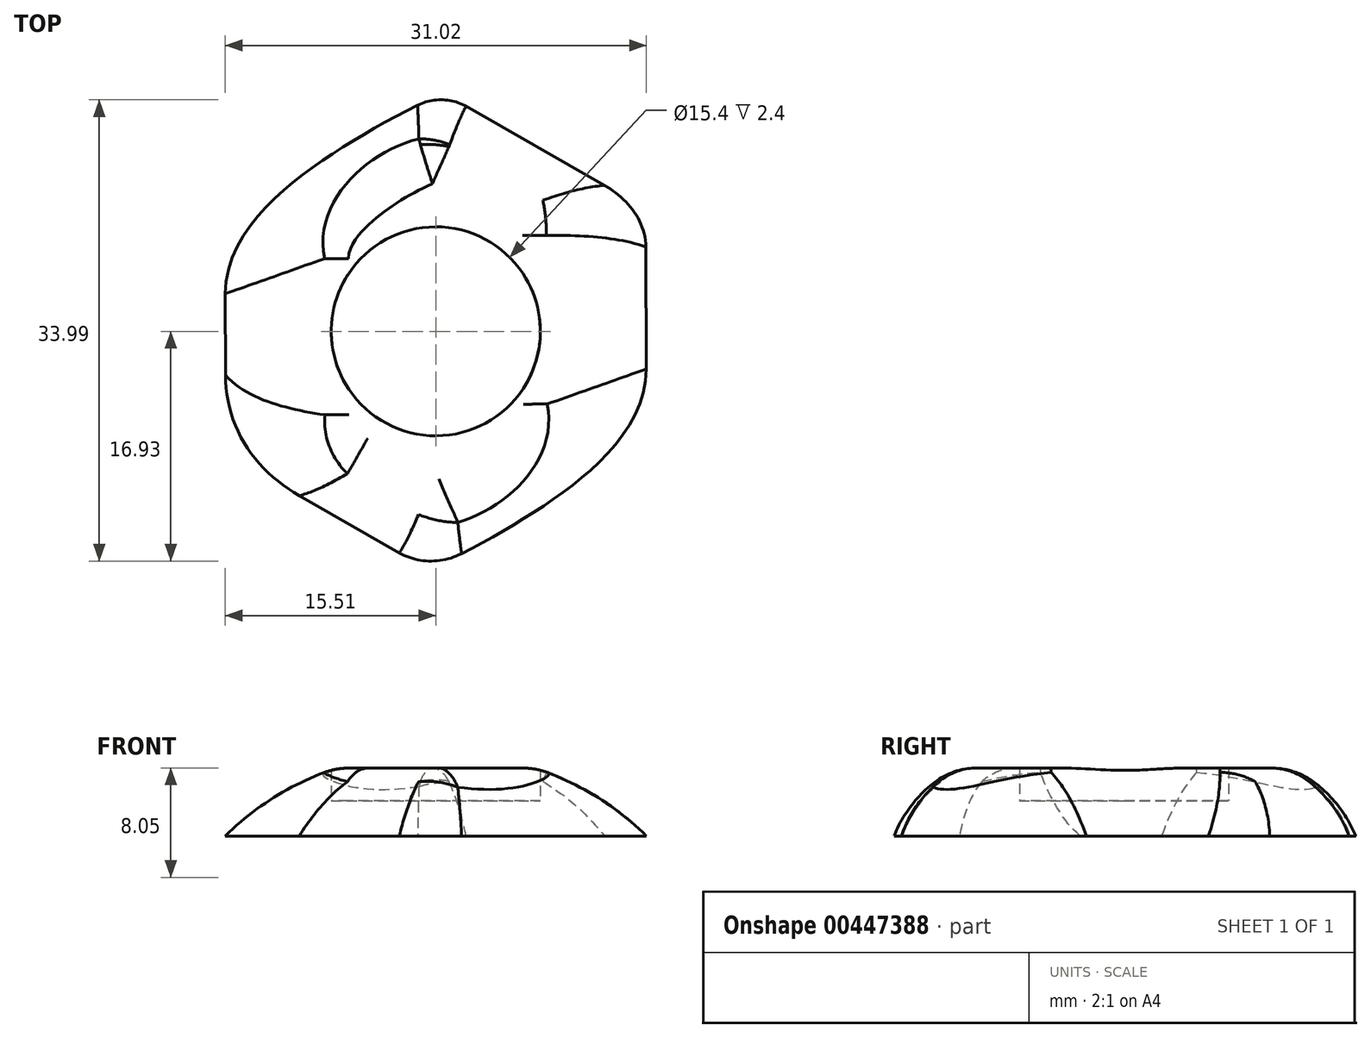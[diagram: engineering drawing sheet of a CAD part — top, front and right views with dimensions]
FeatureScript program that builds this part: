
annotation { "Feature Type Name" : "Feature", "Feature Type Description" : "" }
export const myFeature = defineFeature(function(context is Context, id is Id, definition is map)
    precondition{}
    {
        {
            var Q0;
            Q0=qCreatedBy(makeId("Top.planeOp"),FACE);
            var sketch = newSketch(context, id + "F0", { "sketchPlane" : qUnion([Q0])});
            skCircle(sketch, "E0.cCircle", {"center": v(0, 0) * mm, "radius": 17.9 * mm, "construction": true});
            skLineSegment(sketch, "E0.0", {"start": v(-15.53, 8.9) * mm, "end": v(-0.06, 17.9) * mm});
            skLineSegment(sketch, "E0.1", {"start": v(-0.06, 17.9) * mm, "end": v(15.47, 9) * mm});
            skLineSegment(sketch, "E0.2", {"start": v(15.47, 9) * mm, "end": v(15.53, -8.9) * mm});
            skLineSegment(sketch, "E0.3", {"start": v(15.53, -8.9) * mm, "end": v(0.06, -17.9) * mm});
            skLineSegment(sketch, "E0.4", {"start": v(0.06, -17.9) * mm, "end": v(-15.47, -9) * mm});
            skLineSegment(sketch, "E0.5", {"start": v(-15.47, -9) * mm, "end": v(-15.53, 8.9) * mm});
            skCircle(sketch, "E1", {"center": v(0, 0) * mm, "radius": 7.7 * mm});
            skSolve(sketch);
        }
        {
            var Q0;
            Q0 = qSketchRegion(id + "F0", true);
            extrude(context, id + "F1", {"entities" : qUnion([Q0]), "depth" : 6 * mm});
        }
        {
            var Q0;
            Q0=qCreatedBy(makeId("Top.planeOp"),FACE);
            var sketch = newSketch(context, id + "F2", { "sketchPlane" : qUnion([Q0])});
            skCircle(sketch, "E2", {"center": v(0, 0) * mm, "radius": 12.2 * mm});
            skSolve(sketch);
        }
        {
            var Q0;
            Q0 = qSketchRegion(id + "F2", true);
            extrude(context, id + "F3", {"entities" : qUnion([Q0]), "operationType" : NewBodyOperationType.ADD, "depth" : 2.6 * mm});
        }
        {
            var Q0;
            Q0=makeQuery(id+"F1.opExtrude","CAP_EDGE",EDGE,{"disambiguationData":[OSD([sQuery(id+"F0.wireOp",EDGE,"E0.5")])],"isStart":false});
            fillet(context, id + "F4", {"entities" : qUnion([Q0]), "radius" : 20.76 * mm, "tangentPropagation" : true, "allowEdgeOverflow" : false});
        }
        {
            var Q0;
            Q0=makeQuery(id+"F4.opFillet","BLEND_EDGE",EDGE,{"blendedFrom":[makeQuery(id+"F1.opExtrude","CAP_EDGE",EDGE,{"disambiguationData":[OSD([sQuery(id+"F0.wireOp",EDGE,"E0.5")])],"isStart":false}),makeQuery(id+"F1.opExtrude","SWEPT_FACE",FACE,{"disambiguationData":[OSD([sQuery(id+"F0.wireOp",EDGE,"E0.4")])]})],"blendedInto":[makeQuery(id+"F1.opExtrude","SWEPT_FACE",FACE,{"disambiguationData":[OSD([sQuery(id+"F0.wireOp",EDGE,"E0.4")])]})]});
            fillet(context, id + "F5", {"entities" : qUnion([Q0]), "radius" : 10 * mm, "tangentPropagation" : true, "allowEdgeOverflow" : false});
        }
        {
            var Q0;
            Q0=makeQuery(id+"F1.opExtrude","CAP_EDGE",EDGE,{"disambiguationData":[OSD([sQuery(id+"F0.wireOp",EDGE,"E0.2")])],"isStart":false});
            fillet(context, id + "F6", {"entities" : qUnion([Q0]), "radius" : 20.76 * mm, "tangentPropagation" : true, "allowEdgeOverflow" : false});
        }
        {
            var Q0;
            Q0=makeQuery(id+"F6.opFillet","BLEND_EDGE",EDGE,{"blendedFrom":[makeQuery(id+"F1.opExtrude","CAP_EDGE",EDGE,{"disambiguationData":[OSD([sQuery(id+"F0.wireOp",EDGE,"E0.2")])],"isStart":false}),makeQuery(id+"F1.opExtrude","SWEPT_FACE",FACE,{"disambiguationData":[OSD([sQuery(id+"F0.wireOp",EDGE,"E0.1")])]})],"blendedInto":[makeQuery(id+"F1.opExtrude","SWEPT_FACE",FACE,{"disambiguationData":[OSD([sQuery(id+"F0.wireOp",EDGE,"E0.1")])]})]});
            fillet(context, id + "F7", {"entities" : qUnion([Q0]), "radius" : 10.07 * mm, "tangentPropagation" : true, "allowEdgeOverflow" : false});
        }
        {
            var Q0;
            Q0=makeQuery(id+"F4.opFillet","BLEND_EDGE",EDGE,{"blendedFrom":[makeQuery(id+"F1.opExtrude","CAP_EDGE",EDGE,{"disambiguationData":[OSD([sQuery(id+"F0.wireOp",EDGE,"E0.5")])],"isStart":false}),makeQuery(id+"F1.opExtrude","SWEPT_FACE",FACE,{"disambiguationData":[OSD([sQuery(id+"F0.wireOp",EDGE,"E0.0")])]})],"blendedInto":[makeQuery(id+"F1.opExtrude","SWEPT_FACE",FACE,{"disambiguationData":[OSD([sQuery(id+"F0.wireOp",EDGE,"E0.0")])]})]});
            fillet(context, id + "F8", {"entities" : qUnion([Q0]), "radius" : 8.18 * mm, "tangentPropagation" : true, "allowEdgeOverflow" : false});
        }
        {
            var Q0;
            Q0=makeQuery(id+"F6.opFillet","BLEND_EDGE",EDGE,{"blendedFrom":[makeQuery(id+"F1.opExtrude","CAP_EDGE",EDGE,{"disambiguationData":[OSD([sQuery(id+"F0.wireOp",EDGE,"E0.2")])],"isStart":false}),makeQuery(id+"F1.opExtrude","SWEPT_FACE",FACE,{"disambiguationData":[OSD([sQuery(id+"F0.wireOp",EDGE,"E0.3")])]})],"blendedInto":[makeQuery(id+"F1.opExtrude","SWEPT_FACE",FACE,{"disambiguationData":[OSD([sQuery(id+"F0.wireOp",EDGE,"E0.3")])]})]});
            fillet(context, id + "F9", {"entities" : qUnion([Q0]), "radius" : 8.18 * mm, "tangentPropagation" : true, "allowEdgeOverflow" : false});
        }
        {
            var Q0;
            Q0=makeQuery(id+"F8.opFillet","BLEND_EDGE",EDGE,{"blendedFrom":[makeQuery(id+"F4.opFillet","BLEND_EDGE",EDGE,{"blendedFrom":[makeQuery(id+"F1.opExtrude","CAP_EDGE",EDGE,{"disambiguationData":[OSD([sQuery(id+"F0.wireOp",EDGE,"E0.5")])],"isStart":false}),makeQuery(id+"F1.opExtrude","SWEPT_FACE",FACE,{"disambiguationData":[OSD([sQuery(id+"F0.wireOp",EDGE,"E0.0")])]})],"blendedInto":[makeQuery(id+"F1.opExtrude","SWEPT_FACE",FACE,{"disambiguationData":[OSD([sQuery(id+"F0.wireOp",EDGE,"E0.0")])]})]}),makeQuery(id+"F7.opFillet","BLEND_FACE",FACE,{"disambiguationData":[OSD([sQuery(id+"F0.wireOp",EDGE,"E0.1"),sQuery(id+"F0.wireOp",EDGE,"E0.2")])]})],"blendedInto":[makeQuery(id+"F7.opFillet","BLEND_FACE",FACE,{"disambiguationData":[OSD([sQuery(id+"F0.wireOp",EDGE,"E0.1"),sQuery(id+"F0.wireOp",EDGE,"E0.2")])]})]});
            fillet(context, id + "F10", {"entities" : qUnion([Q0]), "radius" : 4 * mm, "tangentPropagation" : true, "allowEdgeOverflow" : false});
        }
        {
            var Q0;
            Q0=makeQuery(id+"F9.opFillet","BLEND_EDGE",EDGE,{"blendedFrom":[makeQuery(id+"F6.opFillet","BLEND_EDGE",EDGE,{"blendedFrom":[makeQuery(id+"F1.opExtrude","CAP_EDGE",EDGE,{"disambiguationData":[OSD([sQuery(id+"F0.wireOp",EDGE,"E0.2")])],"isStart":false}),makeQuery(id+"F1.opExtrude","SWEPT_FACE",FACE,{"disambiguationData":[OSD([sQuery(id+"F0.wireOp",EDGE,"E0.3")])]})],"blendedInto":[makeQuery(id+"F1.opExtrude","SWEPT_FACE",FACE,{"disambiguationData":[OSD([sQuery(id+"F0.wireOp",EDGE,"E0.3")])]})]}),makeQuery(id+"F5.opFillet","BLEND_FACE",FACE,{"disambiguationData":[OSD([sQuery(id+"F0.wireOp",EDGE,"E0.4"),sQuery(id+"F0.wireOp",EDGE,"E0.5")]),OD(1.0)]})],"blendedInto":[makeQuery(id+"F5.opFillet","BLEND_FACE",FACE,{"disambiguationData":[OSD([sQuery(id+"F0.wireOp",EDGE,"E0.4"),sQuery(id+"F0.wireOp",EDGE,"E0.5")]),OD(1.0)]})]});
            fillet(context, id + "F11", {"entities" : qUnion([Q0]), "radius" : 5 * mm, "tangentPropagation" : true, "allowEdgeOverflow" : false});
        }
        {
            var Q0;
            Q0=makeQuery(id+"F1.opExtrude","SWEPT_BODY",BODY,{"disambiguationData":[OSD([sQuery(id+"F0.wireOp",EDGE,"E0.0"),sQuery(id+"F0.wireOp",EDGE,"E0.1"),sQuery(id+"F0.wireOp",EDGE,"E0.2"),sQuery(id+"F0.wireOp",EDGE,"E0.3"),sQuery(id+"F0.wireOp",EDGE,"E0.4"),sQuery(id+"F0.wireOp",EDGE,"E0.5"),sQuery(id+"F0.wireOp",EDGE,"E1")])]});
            transform(context, id + "F12", {"entities" : qUnion([Q0]), "transformType" : TransformType.TRANSLATION_3D, "dx" : 0.7 * mm, "dy" : 10.2 * mm, "dz" : 7.4 * mm, "makeCopy" : true});
        }
        {
            var Q0;
            Q0=makeQuery(id+"F5.opFillet","BLEND_EDGE",EDGE,{"blendedFrom":[makeQuery(id+"F1.opExtrude","CAP_EDGE",EDGE,{"disambiguationData":[OSD([sQuery(id+"F0.wireOp",EDGE,"E0.4")])],"isStart":false}),makeQuery(id+"F4.opFillet","BLEND_FACE",FACE,{"disambiguationData":[OSD([sQuery(id+"F0.wireOp",EDGE,"E0.5")])]})],"blendedInto":[makeQuery(id+"F4.opFillet","BLEND_FACE",FACE,{"disambiguationData":[OSD([sQuery(id+"F0.wireOp",EDGE,"E0.5")])]})]});
            fillet(context, id + "F13", {"entities" : qUnion([Q0]), "radius" : 7.86 * mm, "tangentPropagation" : true, "allowEdgeOverflow" : false});
        }
        {
            var Q0;
            Q0=makeQuery(id+"F12.opPattern","COPY",BODY,{"derivedFrom":makeQuery(id+"F1.opExtrude","SWEPT_BODY",BODY,{"disambiguationData":[OSD([sQuery(id+"F0.wireOp",EDGE,"E0.0"),sQuery(id+"F0.wireOp",EDGE,"E0.1"),sQuery(id+"F0.wireOp",EDGE,"E0.2"),sQuery(id+"F0.wireOp",EDGE,"E0.3"),sQuery(id+"F0.wireOp",EDGE,"E0.4"),sQuery(id+"F0.wireOp",EDGE,"E0.5"),sQuery(id+"F0.wireOp",EDGE,"E1")])]}),"instanceName":"1"});
            deleteBodies(context, id + "F14", {"entities" : qUnion([Q0])});
        }
        {
            var Q0;
            Q0=makeQuery(id+"F1.opExtrude","SWEPT_BODY",BODY,{"disambiguationData":[OSD([sQuery(id+"F0.wireOp",EDGE,"E0.0"),sQuery(id+"F0.wireOp",EDGE,"E0.1"),sQuery(id+"F0.wireOp",EDGE,"E0.2"),sQuery(id+"F0.wireOp",EDGE,"E0.3"),sQuery(id+"F0.wireOp",EDGE,"E0.4"),sQuery(id+"F0.wireOp",EDGE,"E0.5"),sQuery(id+"F0.wireOp",EDGE,"E1")])]});
            transform(context, id + "F15", {"entities" : qUnion([Q0]), "transformType" : TransformType.TRANSLATION_3D, "dx" : 0 * mm, "dy" : 0 * mm, "dz" : 5 * mm, "makeCopy" : true});
        }
        {
            var Q0;
            Q0=makeQuery(id+"F15.opPattern","COPY",BODY,{"derivedFrom":makeQuery(id+"F1.opExtrude","SWEPT_BODY",BODY,{"disambiguationData":[OSD([sQuery(id+"F0.wireOp",EDGE,"E0.0"),sQuery(id+"F0.wireOp",EDGE,"E0.1"),sQuery(id+"F0.wireOp",EDGE,"E0.2"),sQuery(id+"F0.wireOp",EDGE,"E0.3"),sQuery(id+"F0.wireOp",EDGE,"E0.4"),sQuery(id+"F0.wireOp",EDGE,"E0.5"),sQuery(id+"F0.wireOp",EDGE,"E1")])]}),"instanceName":"1"});
            var Q1;
            Q1=makeQuery(id+"F1.opExtrude","SWEPT_BODY",BODY,{"disambiguationData":[OSD([sQuery(id+"F0.wireOp",EDGE,"E0.0"),sQuery(id+"F0.wireOp",EDGE,"E0.1"),sQuery(id+"F0.wireOp",EDGE,"E0.2"),sQuery(id+"F0.wireOp",EDGE,"E0.3"),sQuery(id+"F0.wireOp",EDGE,"E0.4"),sQuery(id+"F0.wireOp",EDGE,"E0.5"),sQuery(id+"F0.wireOp",EDGE,"E1")])]});
            booleanBodies(context, id + "F16", {"operationType" : BooleanOperationType.SUBTRACTION, "tools" : qUnion([Q0]), "targets" : qUnion([Q1])});
        }
        {
            var Q0;
            {var subQ0=sQuery(id+"F0.wireOp",EDGE,"E0.4");Q0=makeQuery(id+"F16.opBoolean","INTERSECT",EDGE,{"derivedFrom":[makeQuery(id+"F5.opFillet","BLEND_FACE",FACE,{"disambiguationData":[OSD([subQ0])]}),makeQuery(id+"F15.opPattern","COPY",FACE,{"derivedFrom":makeQuery(id+"F3.boolean.opBoolean","MERGE",FACE,{"derivedFrom":[makeQuery(id+"F1.opExtrude","CAP_FACE",FACE,{"disambiguationData":[OSD([sQuery(id+"F0.wireOp",EDGE,"E0.0"),sQuery(id+"F0.wireOp",EDGE,"E0.1"),sQuery(id+"F0.wireOp",EDGE,"E0.2"),sQuery(id+"F0.wireOp",EDGE,"E0.3"),subQ0,sQuery(id+"F0.wireOp",EDGE,"E0.5"),sQuery(id+"F0.wireOp",EDGE,"E1")])],"isStart":true}),makeQuery(id+"F3.opExtrude","CAP_FACE",FACE,{"disambiguationData":[OSD([sQuery(id+"F2.wireOp",EDGE,"E2")])],"isStart":true})]}),"instanceName":"1"})]});}
            fillet(context, id + "F17", {"entities" : qUnion([Q0]), "radius" : 5 * mm, "tangentPropagation" : true, "allowEdgeOverflow" : false});
        }
        {
            var Q0;
            {var subQ0=sQuery(id+"F0.wireOp",EDGE,"E0.5");var subQ1=sQuery(id+"F0.wireOp",EDGE,"E0.0");Q0=makeQuery(id+"F16.opBoolean","INTERSECT",EDGE,{"derivedFrom":[makeQuery(id+"F8.opFillet","BLEND_FACE",FACE,{"disambiguationData":[OSD([subQ1,subQ0])]}),makeQuery(id+"F15.opPattern","COPY",FACE,{"derivedFrom":makeQuery(id+"F3.boolean.opBoolean","MERGE",FACE,{"derivedFrom":[makeQuery(id+"F1.opExtrude","CAP_FACE",FACE,{"disambiguationData":[OSD([subQ1,sQuery(id+"F0.wireOp",EDGE,"E0.1"),sQuery(id+"F0.wireOp",EDGE,"E0.2"),sQuery(id+"F0.wireOp",EDGE,"E0.3"),sQuery(id+"F0.wireOp",EDGE,"E0.4"),subQ0,sQuery(id+"F0.wireOp",EDGE,"E1")])],"isStart":true}),makeQuery(id+"F3.opExtrude","CAP_FACE",FACE,{"disambiguationData":[OSD([sQuery(id+"F2.wireOp",EDGE,"E2")])],"isStart":true})]}),"instanceName":"1"})]});}
            fillet(context, id + "F18", {"entities" : qUnion([Q0]), "radius" : 5 * mm, "tangentPropagation" : true, "allowEdgeOverflow" : false});
        }
    });
